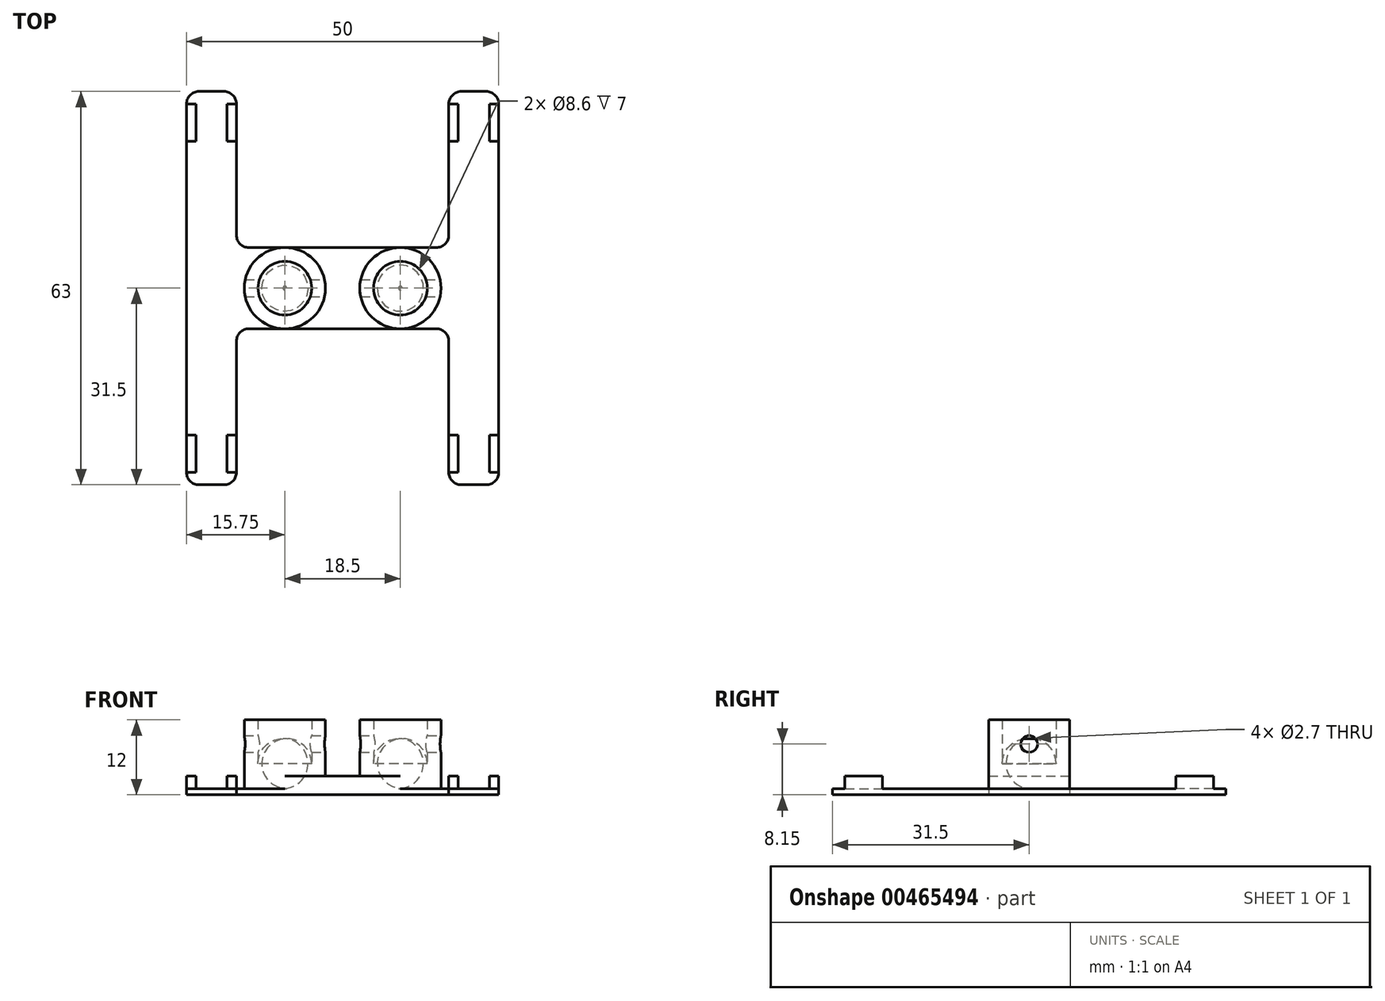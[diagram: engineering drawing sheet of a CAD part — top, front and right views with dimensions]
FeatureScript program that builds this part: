
annotation { "Feature Type Name" : "Feature", "Feature Type Description" : "" }
export const myFeature = defineFeature(function(context is Context, id is Id, definition is map)
    precondition{}
    {
        {
            var Q0;
            Q0=qCreatedBy(makeId("Top.planeOp"),FACE);
            var sketch = newSketch(context, id + "F0", { "sketchPlane" : qUnion([Q0])});
            skLineSegment(sketch, "E0.bottom", {"start": v(0, 0) * mm, "end": v(-50, 0) * mm});
            skLineSegment(sketch, "E0.top", {"start": v(0, 13) * mm, "end": v(-50, 13) * mm});
            skLineSegment(sketch, "E0.left", {"start": v(0, 0) * mm, "end": v(0, 13) * mm});
            skLineSegment(sketch, "E0.right", {"start": v(-50, 0) * mm, "end": v(-50, 13) * mm});
            skLineSegment(sketch, "E1.bottom", {"start": v(-50, 0) * mm, "end": v(-42, 0) * mm});
            skLineSegment(sketch, "E1.top", {"start": v(-50, -25) * mm, "end": v(-42, -25) * mm});
            skLineSegment(sketch, "E1.left", {"start": v(-50, 0) * mm, "end": v(-50, -25) * mm});
            skLineSegment(sketch, "E1.right", {"start": v(-42, 0) * mm, "end": v(-42, -25) * mm});
            skLineSegment(sketch, "E2", {"start": v(-25, 13) * mm, "end": v(-25, 0) * mm, "construction": true});
            skLineSegment(sketch, "E3.MirrorCS", {"start": v(-8, 0) * mm, "end": v(-8, -25) * mm});
            skLineSegment(sketch, "E4.MirrorCS", {"start": v(0, 0) * mm, "end": v(0, -25) * mm});
            skLineSegment(sketch, "E5.MirrorCS", {"start": v(0, -25) * mm, "end": v(-8, -25) * mm});
            skLineSegment(sketch, "E6", {"start": v(-50, 6.5) * mm, "end": v(0, 6.5) * mm, "construction": true});
            skLineSegment(sketch, "E7.MirrorCS", {"start": v(-8, 13) * mm, "end": v(-8, 38) * mm});
            skLineSegment(sketch, "E8.MirrorCS", {"start": v(0, 13) * mm, "end": v(0, 38) * mm});
            skLineSegment(sketch, "E9.MirrorCS", {"start": v(0, 38) * mm, "end": v(-8, 38) * mm});
            skLineSegment(sketch, "E10.MirrorCS", {"start": v(-42, 13) * mm, "end": v(-42, 38) * mm});
            skLineSegment(sketch, "E11.MirrorCS", {"start": v(-50, 13) * mm, "end": v(-50, 38) * mm});
            skLineSegment(sketch, "E12.MirrorCS", {"start": v(-50, 38) * mm, "end": v(-42, 38) * mm});
            skSolve(sketch);
        }
        {
            var Q0;
            Q0 = qSketchRegion(id + "F0", true);
            extrude(context, id + "F1", {"entities" : qUnion([Q0]), "depth" : 1 * mm, "offsetDistance" : 25 * mm});
        }
        {
            var Q0;
            Q0=makeQuery(id+"F1.opExtrude","CAP_FACE",FACE,{"disambiguationData":[OSD([sQuery(id+"F0.wireOp",EDGE,"E0.bottom"),sQuery(id+"F0.wireOp",EDGE,"E0.top"),sQuery(id+"F0.wireOp",EDGE,"E0.left"),sQuery(id+"F0.wireOp",EDGE,"E0.right"),sQuery(id+"F0.wireOp",EDGE,"E1.top"),sQuery(id+"F0.wireOp",EDGE,"E1.left"),sQuery(id+"F0.wireOp",EDGE,"E1.right"),sQuery(id+"F0.wireOp",EDGE,"E3.MirrorCS"),sQuery(id+"F0.wireOp",EDGE,"E4.MirrorCS"),sQuery(id+"F0.wireOp",EDGE,"E5.MirrorCS"),sQuery(id+"F0.wireOp",EDGE,"E7.MirrorCS"),sQuery(id+"F0.wireOp",EDGE,"E8.MirrorCS"),sQuery(id+"F0.wireOp",EDGE,"E9.MirrorCS"),sQuery(id+"F0.wireOp",EDGE,"E10.MirrorCS"),sQuery(id+"F0.wireOp",EDGE,"E11.MirrorCS"),sQuery(id+"F0.wireOp",EDGE,"E12.MirrorCS")])],"isStart":false});
            var sketch = newSketch(context, id + "F2", { "sketchPlane" : qUnion([Q0])});
            skCircle(sketch, "E13", {"center": v(-34.25, 6.5) * mm, "radius": 6.5 * mm});
            skPoint(sketch, "E13.centerSnap0", {"position": v(-50, 6.5) * mm});
            skCircle(sketch, "E14", {"center": v(-34.25, 6.5) * mm, "radius": 4.3 * mm});
            skLineSegment(sketch, "E15", {"start": v(-25, 13) * mm, "end": v(-25, 0) * mm, "construction": true});
            skCircle(sketch, "E16.MirrorC", {"center": v(-15.75, 6.5) * mm, "radius": 6.5 * mm});
            skCircle(sketch, "E17.MirrorC", {"center": v(-15.75, 6.5) * mm, "radius": 4.3 * mm});
            skSolve(sketch);
        }
        {
            var Q0;
            Q0 = qSketchRegion(id + "F2", true);
            extrude(context, id + "F3", {"entities" : qUnion([Q0]), "operationType" : NewBodyOperationType.ADD, "depth" : 11 * mm});
        }
        {
            var Q0;
            Q0=makeQuery(id+"F3.opExtrude","CAP_EDGE",EDGE,{"disambiguationData":[OSD([sQuery(id+"F2.wireOp",EDGE,"E14")])],"isStart":true});
            var Q1;
            Q1=makeQuery(id+"F3.opExtrude","CAP_EDGE",EDGE,{"disambiguationData":[OSD([sQuery(id+"F2.wireOp",EDGE,"E17.MirrorC")])],"isStart":true});
            fillet(context, id + "F4", {"entities" : qUnion([Q0, Q1]), "radius" : 4 * mm, "tangentPropagation" : true, "allowEdgeOverflow" : false});
        }
        {
            var Q0;
            Q0=makeQuery(id+"F1.opExtrude","SWEPT_FACE",FACE,{"disambiguationData":[OSD([sQuery(id+"F0.wireOp",EDGE,"E0.left")])]});
            var sketch = newSketch(context, id + "F5", { "sketchPlane" : qUnion([Q0])});
            skCircle(sketch, "E18", {"center": v(6.5, 8.15) * mm, "radius": 1.35 * mm});
            skSolve(sketch);
        }
        {
            var Q0;
            Q0 = qSketchRegion(id + "F5", true);
            extrude(context, id + "F6", {"entities" : qUnion([Q0]), "operationType" : NewBodyOperationType.REMOVE, "endBound" : BoundingType.THROUGH_ALL, "oppositeDirection" : true, "depth" : 25 * mm});
        }
        {
            var Q0;
            Q0=makeQuery(id+"F1.opExtrude","SWEPT_EDGE",EDGE,{"disambiguationData":[OSD([sQuery(id+"F0.wireOp",EDGE,"E10.MirrorCS"),sQuery(id+"F0.wireOp",EDGE,"E12.MirrorCS")])]});
            var Q1;
            Q1=makeQuery(id+"F1.opExtrude","SWEPT_EDGE",EDGE,{"disambiguationData":[OSD([sQuery(id+"F0.wireOp",EDGE,"E8.MirrorCS"),sQuery(id+"F0.wireOp",EDGE,"E9.MirrorCS")])]});
            var Q2;
            Q2=makeQuery(id+"F1.opExtrude","SWEPT_EDGE",EDGE,{"disambiguationData":[OSD([sQuery(id+"F0.wireOp",EDGE,"E7.MirrorCS"),sQuery(id+"F0.wireOp",EDGE,"E9.MirrorCS")])]});
            var Q3;
            Q3=makeQuery(id+"F1.opExtrude","SWEPT_EDGE",EDGE,{"disambiguationData":[OSD([sQuery(id+"F0.wireOp",EDGE,"E0.top"),sQuery(id+"F0.wireOp",EDGE,"E0.left")])]});
            var Q4;
            Q4=makeQuery(id+"F1.opExtrude","SWEPT_EDGE",EDGE,{"disambiguationData":[OSD([sQuery(id+"F0.wireOp",EDGE,"E0.bottom"),sQuery(id+"F0.wireOp",EDGE,"E0.left")])]});
            var Q5;
            Q5=makeQuery(id+"F1.opExtrude","SWEPT_EDGE",EDGE,{"disambiguationData":[OSD([sQuery(id+"F0.wireOp",EDGE,"E0.bottom"),sQuery(id+"F0.wireOp",EDGE,"E4.MirrorCS")])]});
            var Q6;
            Q6=makeQuery(id+"F1.opExtrude","SWEPT_EDGE",EDGE,{"disambiguationData":[OSD([sQuery(id+"F0.wireOp",EDGE,"E0.top"),sQuery(id+"F0.wireOp",EDGE,"E8.MirrorCS")])]});
            var Q7;
            Q7=makeQuery(id+"F1.opExtrude","SWEPT_EDGE",EDGE,{"disambiguationData":[OSD([sQuery(id+"F0.wireOp",EDGE,"E4.MirrorCS"),sQuery(id+"F0.wireOp",EDGE,"E5.MirrorCS")])]});
            var Q8;
            Q8=makeQuery(id+"F1.opExtrude","SWEPT_EDGE",EDGE,{"disambiguationData":[OSD([sQuery(id+"F0.wireOp",EDGE,"E3.MirrorCS"),sQuery(id+"F0.wireOp",EDGE,"E5.MirrorCS")])]});
            var Q9;
            Q9=makeQuery(id+"F1.opExtrude","SWEPT_EDGE",EDGE,{"disambiguationData":[OSD([sQuery(id+"F0.wireOp",EDGE,"E0.bottom"),sQuery(id+"F0.wireOp",EDGE,"E3.MirrorCS")])]});
            var Q10;
            Q10=makeQuery(id+"F1.opExtrude","SWEPT_EDGE",EDGE,{"disambiguationData":[OSD([sQuery(id+"F0.wireOp",EDGE,"E0.bottom"),sQuery(id+"F0.wireOp",EDGE,"E1.bottom"),sQuery(id+"F0.wireOp",EDGE,"E1.right")])]});
            var Q11;
            Q11=makeQuery(id+"F1.opExtrude","SWEPT_EDGE",EDGE,{"disambiguationData":[OSD([sQuery(id+"F0.wireOp",EDGE,"E1.top"),sQuery(id+"F0.wireOp",EDGE,"E1.right")])]});
            var Q12;
            Q12=makeQuery(id+"F1.opExtrude","SWEPT_EDGE",EDGE,{"disambiguationData":[OSD([sQuery(id+"F0.wireOp",EDGE,"E1.top"),sQuery(id+"F0.wireOp",EDGE,"E1.left")])]});
            var Q13;
            Q13=makeQuery(id+"F1.opExtrude","SWEPT_EDGE",EDGE,{"disambiguationData":[OSD([sQuery(id+"F0.wireOp",EDGE,"E0.bottom"),sQuery(id+"F0.wireOp",EDGE,"E1.bottom"),sQuery(id+"F0.wireOp",EDGE,"E1.left")])]});
            var Q14;
            Q14=makeQuery(id+"F1.opExtrude","SWEPT_EDGE",EDGE,{"disambiguationData":[OSD([sQuery(id+"F0.wireOp",EDGE,"E0.bottom"),sQuery(id+"F0.wireOp",EDGE,"E0.right")])]});
            var Q15;
            Q15=makeQuery(id+"F1.opExtrude","SWEPT_EDGE",EDGE,{"disambiguationData":[OSD([sQuery(id+"F0.wireOp",EDGE,"E0.top"),sQuery(id+"F0.wireOp",EDGE,"E0.right")])]});
            var Q16;
            Q16=makeQuery(id+"F1.opExtrude","SWEPT_EDGE",EDGE,{"disambiguationData":[OSD([sQuery(id+"F0.wireOp",EDGE,"E0.top"),sQuery(id+"F0.wireOp",EDGE,"E11.MirrorCS")])]});
            var Q17;
            Q17=makeQuery(id+"F1.opExtrude","SWEPT_EDGE",EDGE,{"disambiguationData":[OSD([sQuery(id+"F0.wireOp",EDGE,"E11.MirrorCS"),sQuery(id+"F0.wireOp",EDGE,"E12.MirrorCS")])]});
            var Q18;
            Q18=makeQuery(id+"F1.opExtrude","SWEPT_EDGE",EDGE,{"disambiguationData":[OSD([sQuery(id+"F0.wireOp",EDGE,"E0.top"),sQuery(id+"F0.wireOp",EDGE,"E10.MirrorCS")])]});
            fillet(context, id + "F7", {"entities" : qUnion([Q0, Q1, Q2, Q3, Q4, Q5, Q6, Q7, Q8, Q9, Q10, Q11, Q12, Q13, Q14, Q15, Q16, Q17, Q18]), "radius" : 2 * mm, "tangentPropagation" : true, "allowEdgeOverflow" : false});
        }
        {
            var Q0;
            {var subQ0=sQuery(id+"F0.wireOp",EDGE,"E1.top");var subQ1=sQuery(id+"F0.wireOp",EDGE,"E0.right");var subQ2=sQuery(id+"F0.wireOp",EDGE,"E0.left");var subQ3=sQuery(id+"F0.wireOp",EDGE,"E0.top");var subQ4=sQuery(id+"F0.wireOp",EDGE,"E11.MirrorCS");var subQ5=sQuery(id+"F0.wireOp",EDGE,"E7.MirrorCS");var subQ6=sQuery(id+"F0.wireOp",EDGE,"E10.MirrorCS");var subQ7=sQuery(id+"F0.wireOp",EDGE,"E1.left");var subQ8=sQuery(id+"F0.wireOp",EDGE,"E0.bottom");var subQ9=sQuery(id+"F0.wireOp",EDGE,"E4.MirrorCS");var subQ10=sQuery(id+"F0.wireOp",EDGE,"E8.MirrorCS");var subQ11=sQuery(id+"F0.wireOp",EDGE,"E1.right");var subQ13=sQuery(id+"F0.wireOp",EDGE,"E3.MirrorCS");var subQ14=sQuery(id+"F0.wireOp",EDGE,"E5.MirrorCS");var subQ15=sQuery(id+"F0.wireOp",EDGE,"E9.MirrorCS");var subQ16=sQuery(id+"F0.wireOp",EDGE,"E12.MirrorCS");Q0=makeQuery(id+"F3.boolean.opBoolean","SPLIT",FACE,{"disambiguationData":[TD([makeQuery(id+"F1.opExtrude","SWEPT_FACE",FACE,{"disambiguationData":[OSD([subQ2])]})])],"derivedFrom":makeQuery(id+"F1.opExtrude","CAP_FACE",FACE,{"disambiguationData":[OSD([subQ8,subQ3,subQ2,subQ1,subQ0,subQ7,subQ11,subQ13,subQ9,subQ14,subQ5,subQ10,subQ15,subQ6,subQ4,subQ16])],"isStart":false})});}
            var sketch = newSketch(context, id + "F8", { "sketchPlane" : qUnion([Q0])});
            skLineSegment(sketch, "E19", {"start": v(-50, 6.5) * mm, "end": v(0, 6.5) * mm, "construction": true});
            skLineSegment(sketch, "E20", {"start": v(-25, 13) * mm, "end": v(-25, 0) * mm, "construction": true});
            skLineSegment(sketch, "E21", {"start": v(-46, 38) * mm, "end": v(-46, -25) * mm, "construction": true});
            skLineSegment(sketch, "E22.bottom", {"start": v(-50, 36) * mm, "end": v(-48.5, 36) * mm});
            skLineSegment(sketch, "E22.top", {"start": v(-50, 30) * mm, "end": v(-48.5, 30) * mm});
            skLineSegment(sketch, "E22.left", {"start": v(-50, 36) * mm, "end": v(-50, 30) * mm});
            skLineSegment(sketch, "E22.right", {"start": v(-48.5, 36) * mm, "end": v(-48.5, 30) * mm});
            skLineSegment(sketch, "E23.MirrorCS", {"start": v(-43.5, 36) * mm, "end": v(-43.5, 30) * mm});
            skLineSegment(sketch, "E24.MirrorCS", {"start": v(-42, 36) * mm, "end": v(-43.5, 36) * mm});
            skLineSegment(sketch, "E25.MirrorCS", {"start": v(-42, 36) * mm, "end": v(-42, 30) * mm});
            skLineSegment(sketch, "E26.MirrorCS", {"start": v(-42, 30) * mm, "end": v(-43.5, 30) * mm});
            skLineSegment(sketch, "E27.MirrorCS", {"start": v(-42, -23) * mm, "end": v(-43.5, -23) * mm});
            skLineSegment(sketch, "E28.MirrorCS", {"start": v(-43.5, -23) * mm, "end": v(-43.5, -17) * mm});
            skLineSegment(sketch, "E29.MirrorCS", {"start": v(-42, -23) * mm, "end": v(-42, -17) * mm});
            skLineSegment(sketch, "E30.MirrorCS", {"start": v(-42, -17) * mm, "end": v(-43.5, -17) * mm});
            skLineSegment(sketch, "E31.MirrorCS", {"start": v(-48.5, -23) * mm, "end": v(-48.5, -17) * mm});
            skLineSegment(sketch, "E32.MirrorCS", {"start": v(-50, -23) * mm, "end": v(-48.5, -23) * mm});
            skLineSegment(sketch, "E33.MirrorCS", {"start": v(-50, -23) * mm, "end": v(-50, -17) * mm});
            skLineSegment(sketch, "E34.MirrorCS", {"start": v(-50, -17) * mm, "end": v(-48.5, -17) * mm});
            skLineSegment(sketch, "E35.MirrorCS", {"start": v(0, 36) * mm, "end": v(-1.5, 36) * mm});
            skLineSegment(sketch, "E36.MirrorCS", {"start": v(-1.5, 36) * mm, "end": v(-1.5, 30) * mm});
            skLineSegment(sketch, "E37.MirrorCS", {"start": v(0, 30) * mm, "end": v(-1.5, 30) * mm});
            skLineSegment(sketch, "E38.MirrorCS", {"start": v(0, 36) * mm, "end": v(0, 30) * mm});
            skLineSegment(sketch, "E39.MirrorCS", {"start": v(-8, 30) * mm, "end": v(-6.5, 30) * mm});
            skLineSegment(sketch, "E40.MirrorCS", {"start": v(-6.5, 36) * mm, "end": v(-6.5, 30) * mm});
            skLineSegment(sketch, "E41.MirrorCS", {"start": v(-8, 36) * mm, "end": v(-8, 30) * mm});
            skLineSegment(sketch, "E42.MirrorCS", {"start": v(-8, 36) * mm, "end": v(-6.5, 36) * mm});
            skLineSegment(sketch, "E43.MirrorCS", {"start": v(-8, -23) * mm, "end": v(-6.5, -23) * mm});
            skLineSegment(sketch, "E44.MirrorCS", {"start": v(0, -17) * mm, "end": v(-1.5, -17) * mm});
            skLineSegment(sketch, "E45.MirrorCS", {"start": v(-8, -17) * mm, "end": v(-6.5, -17) * mm});
            skLineSegment(sketch, "E46.MirrorCS", {"start": v(0, -23) * mm, "end": v(-1.5, -23) * mm});
            skLineSegment(sketch, "E47.MirrorCS", {"start": v(-6.5, -23) * mm, "end": v(-6.5, -17) * mm});
            skLineSegment(sketch, "E48.MirrorCS", {"start": v(-1.5, -23) * mm, "end": v(-1.5, -17) * mm});
            skLineSegment(sketch, "E49.MirrorCS", {"start": v(0, -23) * mm, "end": v(0, -17) * mm});
            skLineSegment(sketch, "E50.MirrorCS", {"start": v(-8, -23) * mm, "end": v(-8, -17) * mm});
            skSolve(sketch);
        }
        {
            var Q0;
            Q0 = qSketchRegion(id + "F8", true);
            extrude(context, id + "F9", {"entities" : qUnion([Q0]), "operationType" : NewBodyOperationType.ADD, "depth" : 2 * mm});
        }
        {
            var Q0;
            {var subQ0=sQuery(id+"F0.wireOp",EDGE,"E0.top");var subQ1=sQuery(id+"F0.wireOp",EDGE,"E0.bottom");var subQ2=makeQuery(id+"F1.opExtrude","CAP_FACE",FACE,{"disambiguationData":[OSD([subQ1,subQ0,sQuery(id+"F0.wireOp",EDGE,"E0.left"),sQuery(id+"F0.wireOp",EDGE,"E0.right"),sQuery(id+"F0.wireOp",EDGE,"E1.top"),sQuery(id+"F0.wireOp",EDGE,"E1.left"),sQuery(id+"F0.wireOp",EDGE,"E1.right"),sQuery(id+"F0.wireOp",EDGE,"E3.MirrorCS"),sQuery(id+"F0.wireOp",EDGE,"E4.MirrorCS"),sQuery(id+"F0.wireOp",EDGE,"E5.MirrorCS"),sQuery(id+"F0.wireOp",EDGE,"E7.MirrorCS"),sQuery(id+"F0.wireOp",EDGE,"E8.MirrorCS"),sQuery(id+"F0.wireOp",EDGE,"E9.MirrorCS"),sQuery(id+"F0.wireOp",EDGE,"E10.MirrorCS"),sQuery(id+"F0.wireOp",EDGE,"E11.MirrorCS"),sQuery(id+"F0.wireOp",EDGE,"E12.MirrorCS")])],"isStart":false});Q0=makeQuery(id+"F3.boolean.opBoolean","SPLIT",FACE,{"disambiguationData":[TD([makeQuery(id+"F1.opExtrude","SWEPT_FACE",FACE,{"disambiguationData":[OSD([subQ1])]}),subQ2,makeQuery(id+"F1.opExtrude","SWEPT_FACE",FACE,{"disambiguationData":[OSD([subQ0])]}),makeQuery(id+"F3.opExtrude","SWEPT_FACE",FACE,{"disambiguationData":[OSD([sQuery(id+"F2.wireOp",EDGE,"E13")])]}),makeQuery(id+"F3.opExtrude","SWEPT_FACE",FACE,{"disambiguationData":[OSD([sQuery(id+"F2.wireOp",EDGE,"E16.MirrorC")])]})])],"derivedFrom":subQ2});}
            var sketch = newSketch(context, id + "F10", { "sketchPlane" : qUnion([Q0])});
            skLineSegment(sketch, "E51", {"start": v(-34.25, 13) * mm, "end": v(-15.75, 13) * mm});
            skLineSegment(sketch, "E52", {"start": v(-34.25, 0) * mm, "end": v(-15.75, 0) * mm});
            skArc(sketch, "E53", {"start": v(-15.75, 13) * mm, "mid": v(-22.25, 6.5) * mm, "end": v(-15.75, 0) * mm});
            skArc(sketch, "E54", {"start": v(-34.25, 0) * mm, "mid": v(-27.75, 6.5) * mm, "end": v(-34.25, 13) * mm});
            skSolve(sketch);
        }
        {
            var Q0;
            Q0 = qSketchRegion(id + "F10", true);
            extrude(context, id + "F11", {"entities" : qUnion([Q0]), "operationType" : NewBodyOperationType.ADD, "depth" : 2 * mm, "offsetDistance" : 25 * mm});
        }
    });
